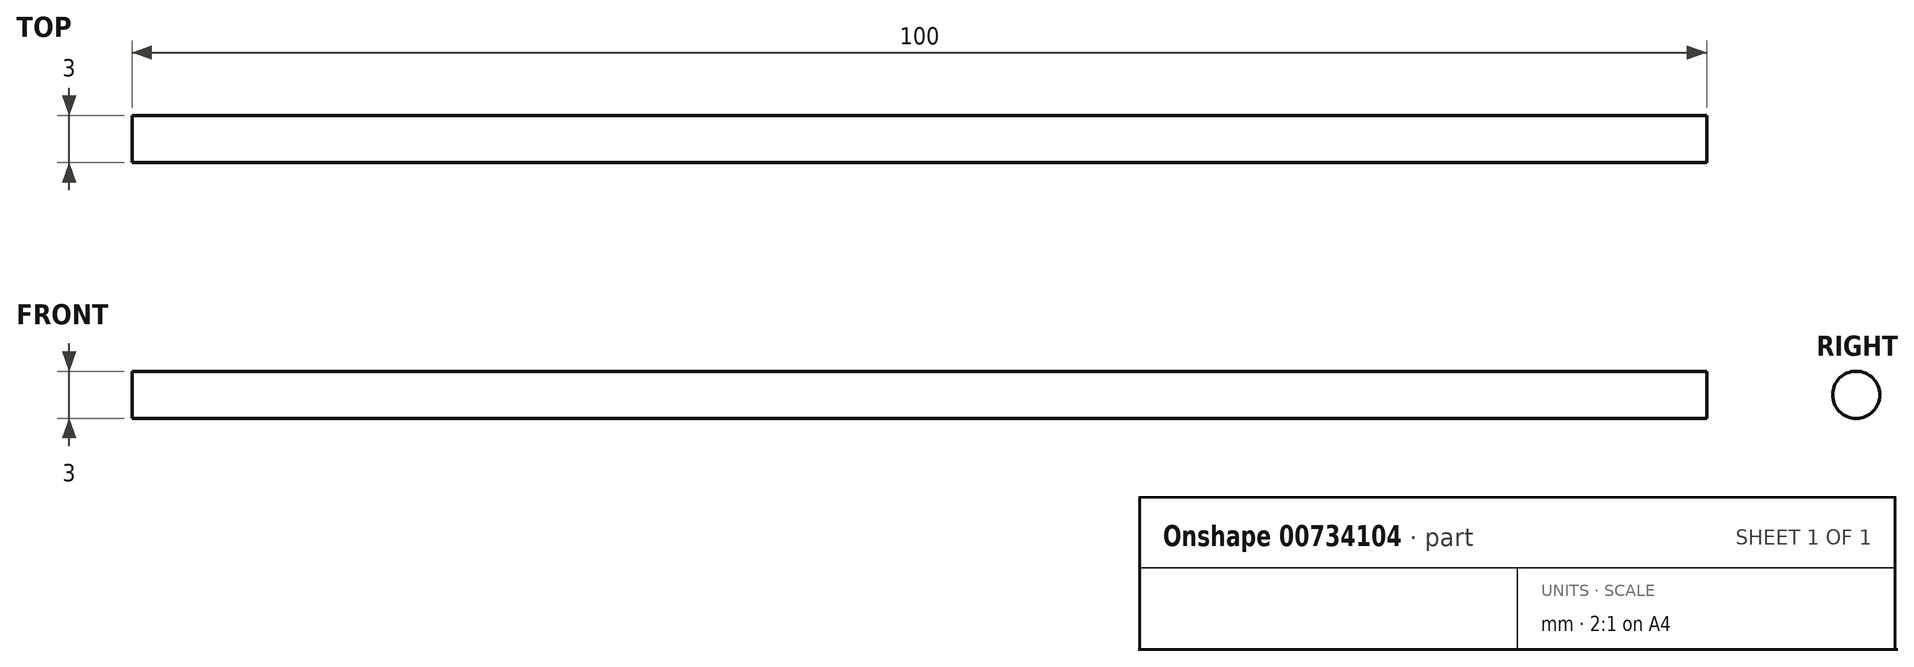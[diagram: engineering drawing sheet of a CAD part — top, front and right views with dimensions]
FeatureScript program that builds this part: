
annotation { "Feature Type Name" : "Feature", "Feature Type Description" : "" }
export const myFeature = defineFeature(function(context is Context, id is Id, definition is map)
    precondition{}
    {
        {
            var Q0;
            Q0=qCreatedBy(makeId("Right.planeOp"),FACE);
            var sketch = newSketch(context, id + "F0", { "sketchPlane" : qUnion([Q0])});
            skCircle(sketch, "E0", {"center": v(-26.28, 22.9) * mm, "radius": 1.5 * mm});
            skSolve(sketch);
        }
        {
            var Q0;
            Q0=makeQuery(id+"F0.imprint","IMPRINT",FACE,{"disambiguationData":[TD([[makeQuery(id+"F0.imprint","IMPRINT",EDGE,{"derivedFrom":sQuery(id+"F0.wireOp",EDGE,"E0")}),1.0]])]});
            extrude(context, id + "F1", {"entities" : qUnion([Q0]), "depth" : 100 * mm, "offsetDistance" : 25 * mm});
        }
    });
